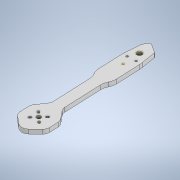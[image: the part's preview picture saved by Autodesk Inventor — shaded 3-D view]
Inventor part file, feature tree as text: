
AUTODESK INVENTOR PART (.ipt)
format: ipt  version: 2020 (Build 240168000, 168)  size: 167,936 bytes
history: native  units: mm
features: other x2, sketch x1
ambient origin geometry x8: Origin, YZ Plane, XZ Plane, XY Plane, X Axis, Y Axis, Z Axis, Center Point
bodies: Solid1 (feature_tree)
feature tree (3):
  other  "froggy arm assm.iam"
  other  "og kauri arm.ipt:1"
  sketch  "Sketch2"  dims[d0=10.0mm]
